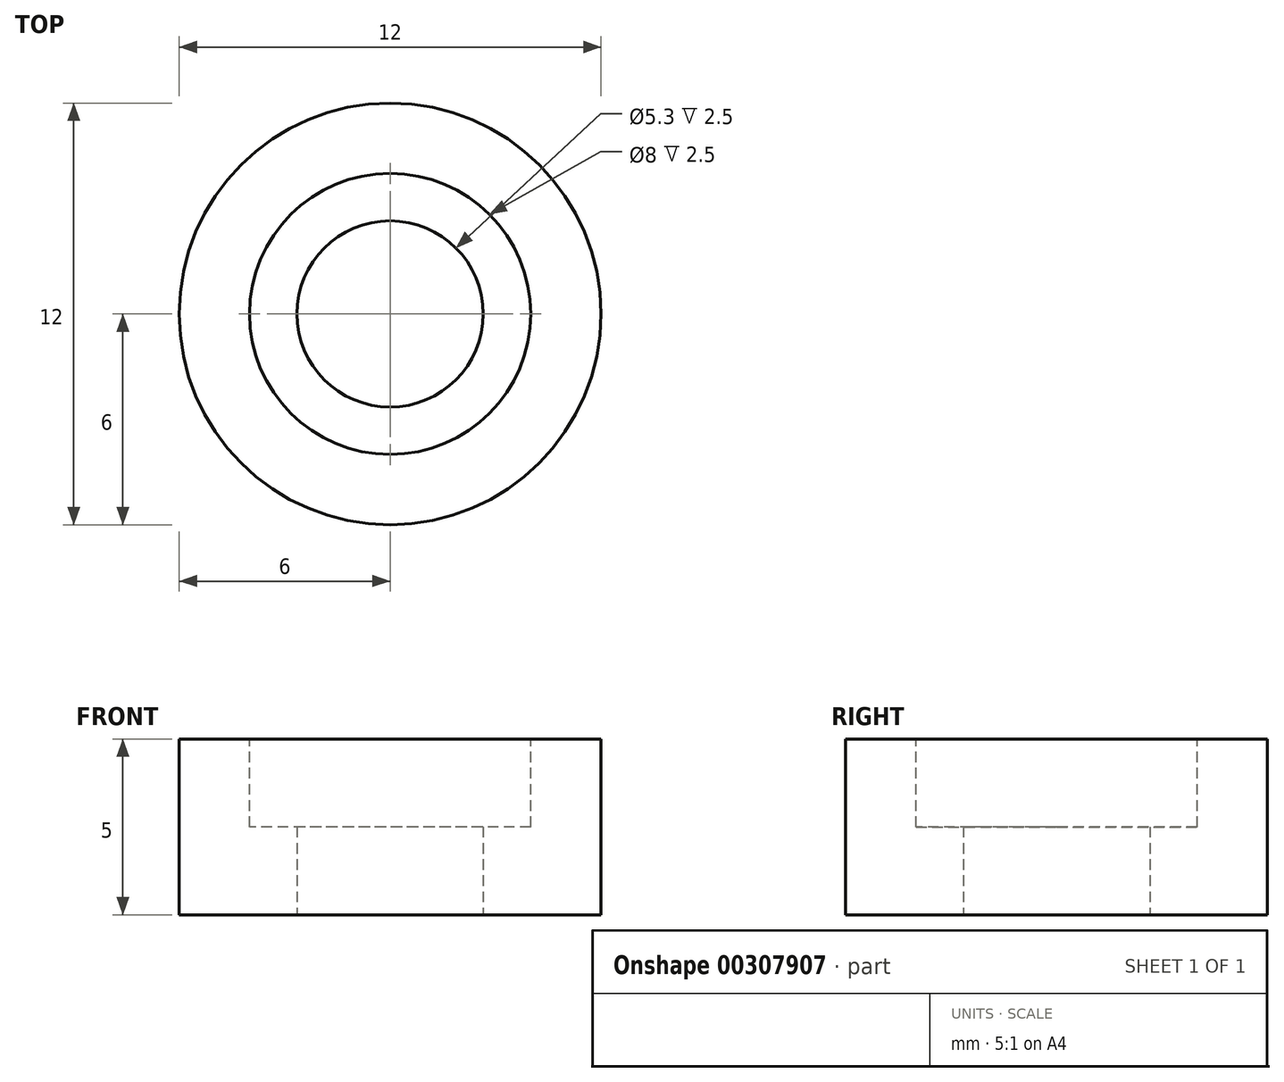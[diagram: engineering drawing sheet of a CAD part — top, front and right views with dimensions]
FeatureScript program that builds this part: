
annotation { "Feature Type Name" : "Feature", "Feature Type Description" : "" }
export const myFeature = defineFeature(function(context is Context, id is Id, definition is map)
    precondition{}
    {
        {
            var Q0;
            Q0=qCreatedBy(makeId("Top.planeOp"),FACE);
            var sketch = newSketch(context, id + "F0", { "sketchPlane" : qUnion([Q0])});
            skCircle(sketch, "E0", {"center": v(0, 0) * mm, "radius": 2.65 * mm});
            skCircle(sketch, "E1", {"center": v(0, 0) * mm, "radius": 6 * mm});
            skSolve(sketch);
        }
        {
            var Q0;
            Q0=makeQuery(id+"F0.imprint","IMPRINT",FACE,{"disambiguationData":[TD([[makeQuery(id+"F0.imprint","IMPRINT",EDGE,{"derivedFrom":sQuery(id+"F0.wireOp",EDGE,"E0")}),-1.0]])]});
            var Q1;
            Q1=makeQuery(id+"F0.imprint","IMPRINT",FACE,{"disambiguationData":[TD([[makeQuery(id+"F0.imprint","IMPRINT",EDGE,{"derivedFrom":sQuery(id+"F0.wireOp",EDGE,"E0")}),1.0]])]});
            extrude(context, id + "F1", {"entities" : qUnion([Q0, Q1]), "depth" : 5 * mm});
        }
        {
            var Q0;
            Q0=makeQuery(id+"F1.opExtrude","CAP_FACE",FACE,{"disambiguationData":[OSD([sQuery(id+"F0.wireOp",EDGE,"E1")])],"isStart":true});
            var sketch = newSketch(context, id + "F2", { "sketchPlane" : qUnion([Q0])});
            skCircle(sketch, "E2.0.0", {"center": v(0, 0) * mm, "radius": 6 * mm});
            skCircle(sketch, "E3", {"center": v(0, 0) * mm, "radius": 2.65 * mm});
            skSolve(sketch);
        }
        {
            var Q0;
            Q0=makeQuery(id+"F2.imprint","IMPRINT",FACE,{"disambiguationData":[TD([[makeQuery(id+"F2.imprint","IMPRINT",EDGE,{"derivedFrom":sQuery(id+"F2.wireOp",EDGE,"E3")}),1.0]])]});
            extrude(context, id + "F3", {"entities" : qUnion([Q0]), "operationType" : NewBodyOperationType.REMOVE, "oppositeDirection" : true, "depth" : 25 * mm});
        }
        {
            var Q0;
            Q0=makeQuery(id+"F1.opExtrude","CAP_FACE",FACE,{"disambiguationData":[OSD([sQuery(id+"F0.wireOp",EDGE,"E1")])],"isStart":false});
            var sketch = newSketch(context, id + "F4", { "sketchPlane" : qUnion([Q0])});
            skCircle(sketch, "E4.0.0", {"center": v(0, 0) * mm, "radius": 6 * mm});
            skCircle(sketch, "E5", {"center": v(0, 0) * mm, "radius": 4 * mm});
            skSolve(sketch);
        }
        {
            var Q0;
            Q0=makeQuery(id+"F4.imprint","IMPRINT",FACE,{"disambiguationData":[TD([[makeQuery(id+"F4.imprint","IMPRINT",EDGE,{"derivedFrom":sQuery(id+"F4.wireOp",EDGE,"E5")}),1.0]])]});
            extrude(context, id + "F5", {"entities" : qUnion([Q0]), "operationType" : NewBodyOperationType.REMOVE, "oppositeDirection" : true, "depth" : 2.5 * mm});
        }
    });
